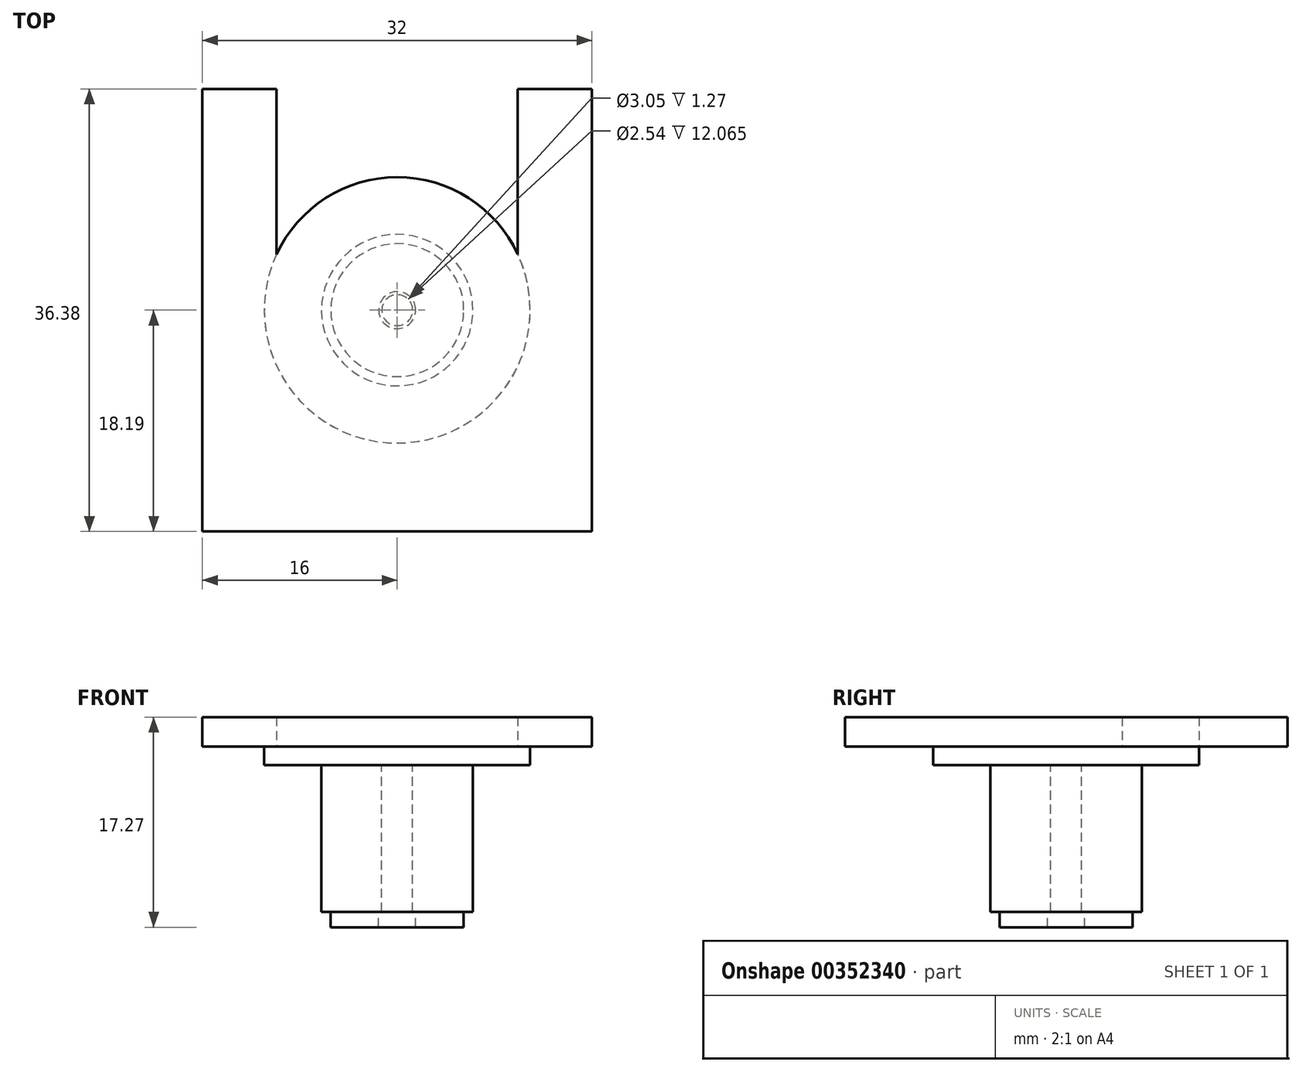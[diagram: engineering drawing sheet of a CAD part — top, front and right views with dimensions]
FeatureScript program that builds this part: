
annotation { "Feature Type Name" : "Feature", "Feature Type Description" : "" }
export const myFeature = defineFeature(function(context is Context, id is Id, definition is map)
    precondition{}
    {
        {
            var Q0;
            Q0=qCreatedBy(makeId("Top.planeOp"),FACE);
            var sketch = newSketch(context, id + "F0", { "sketchPlane" : qUnion([Q0])});
            skCircle(sketch, "E0", {"center": v(0, 0) * mm, "radius": 10.92 * mm, "construction": true});
            skLineSegment(sketch, "E1.bottom", {"start": v(16, -18.19) * mm, "end": v(-16, -18.19) * mm});
            skLineSegment(sketch, "E1.left", {"start": v(16, -18.19) * mm, "end": v(16, 18.19) * mm});
            skLineSegment(sketch, "E1.right", {"start": v(-16, -18.19) * mm, "end": v(-16, 18.19) * mm});
            skLineSegment(sketch, "E2", {"start": v(16, 18.19) * mm, "end": v(9.9, 18.19) * mm});
            skLineSegment(sketch, "E3", {"start": v(9.9, 18.19) * mm, "end": v(9.9, 4.6) * mm});
            skArc(sketch, "E4", {"start": v(9.9, 4.6) * mm, "mid": v(5.88, 9.2) * mm, "end": v(0, 10.92) * mm});
            skArc(sketch, "E5.MirrorCS", {"start": v(-9.9, 4.6) * mm, "mid": v(-5.88, 9.2) * mm, "end": v(0, 10.92) * mm});
            skLineSegment(sketch, "E6.MirrorCS", {"start": v(-9.9, 18.19) * mm, "end": v(-9.9, 4.6) * mm});
            skLineSegment(sketch, "E7.MirrorCS", {"start": v(-16, 18.19) * mm, "end": v(-9.9, 18.19) * mm});
            skSolve(sketch);
        }
        {
            var Q0;
            Q0=makeQuery(id+"F0.imprint","IMPRINT",FACE,{"disambiguationData":[TD([[makeQuery(id+"F0.imprint","IMPRINT",EDGE,{"derivedFrom":sQuery(id+"F0.wireOp",EDGE,"E1.bottom")}),-1.0]])]});
            extrude(context, id + "F1", {"entities" : qUnion([Q0]), "depth" : 2.41 * mm});
        }
        {
            var Q0;
            Q0=makeQuery(id+"F1.opExtrude","CAP_FACE",FACE,{"disambiguationData":[OSD([sQuery(id+"F0.wireOp",EDGE,"E1.bottom"),sQuery(id+"F0.wireOp",EDGE,"E1.left"),sQuery(id+"F0.wireOp",EDGE,"E1.right"),sQuery(id+"F0.wireOp",EDGE,"E2"),sQuery(id+"F0.wireOp",EDGE,"E3"),sQuery(id+"F0.wireOp",EDGE,"E4"),sQuery(id+"F0.wireOp",EDGE,"E5.MirrorCS"),sQuery(id+"F0.wireOp",EDGE,"E6.MirrorCS"),sQuery(id+"F0.wireOp",EDGE,"E7.MirrorCS")])],"isStart":true});
            var sketch = newSketch(context, id + "F2", { "sketchPlane" : qUnion([Q0])});
            skCircle(sketch, "E8", {"center": v(0, 0) * mm, "radius": 10.92 * mm});
            skSolve(sketch);
        }
        {
            var Q0;
            Q0=qSketchRegion(id+"F2",true);
            extrude(context, id + "F3", {"entities" : qUnion([Q0]), "operationType" : NewBodyOperationType.ADD, "depth" : 1.52 * mm});
        }
        {
            var Q0;
            Q0=makeQuery(id+"F3.opExtrude","CAP_FACE",FACE,{"disambiguationData":[OSD([sQuery(id+"F2.wireOp",EDGE,"E8")])],"isStart":false});
            var sketch = newSketch(context, id + "F4", { "sketchPlane" : qUnion([Q0])});
            skCircle(sketch, "E9", {"center": v(0, 0) * mm, "radius": 6.22 * mm});
            skCircle(sketch, "E10", {"center": v(0, 0) * mm, "radius": 1.27 * mm});
            skSolve(sketch);
        }
        {
            var Q0;
            Q0=makeQuery(id+"F4.imprint","IMPRINT",FACE,{"disambiguationData":[TD([[makeQuery(id+"F4.imprint","IMPRINT",EDGE,{"derivedFrom":sQuery(id+"F4.wireOp",EDGE,"E9")}),1.0]])]});
            extrude(context, id + "F5", {"entities" : qUnion([Q0]), "operationType" : NewBodyOperationType.ADD, "depth" : 12.06 * mm});
        }
        {
            var Q0;
            Q0=makeQuery(id+"F5.opExtrude","CAP_FACE",FACE,{"disambiguationData":[OSD([sQuery(id+"F4.wireOp",EDGE,"E9"),sQuery(id+"F4.wireOp",EDGE,"E10")])],"isStart":false});
            var sketch = newSketch(context, id + "F6", { "sketchPlane" : qUnion([Q0])});
            skCircle(sketch, "E11", {"center": v(0, 0) * mm, "radius": 5.46 * mm});
            skCircle(sketch, "E12", {"center": v(0, 0) * mm, "radius": 1.52 * mm});
            skSolve(sketch);
        }
        {
            var Q0;
            Q0=makeQuery(id+"F6.imprint","IMPRINT",FACE,{"disambiguationData":[TD([[makeQuery(id+"F6.imprint","IMPRINT",EDGE,{"derivedFrom":sQuery(id+"F6.wireOp",EDGE,"E11")}),1.0]])]});
            extrude(context, id + "F7", {"entities" : qUnion([Q0]), "operationType" : NewBodyOperationType.ADD, "depth" : 1.27 * mm});
        }
    });
